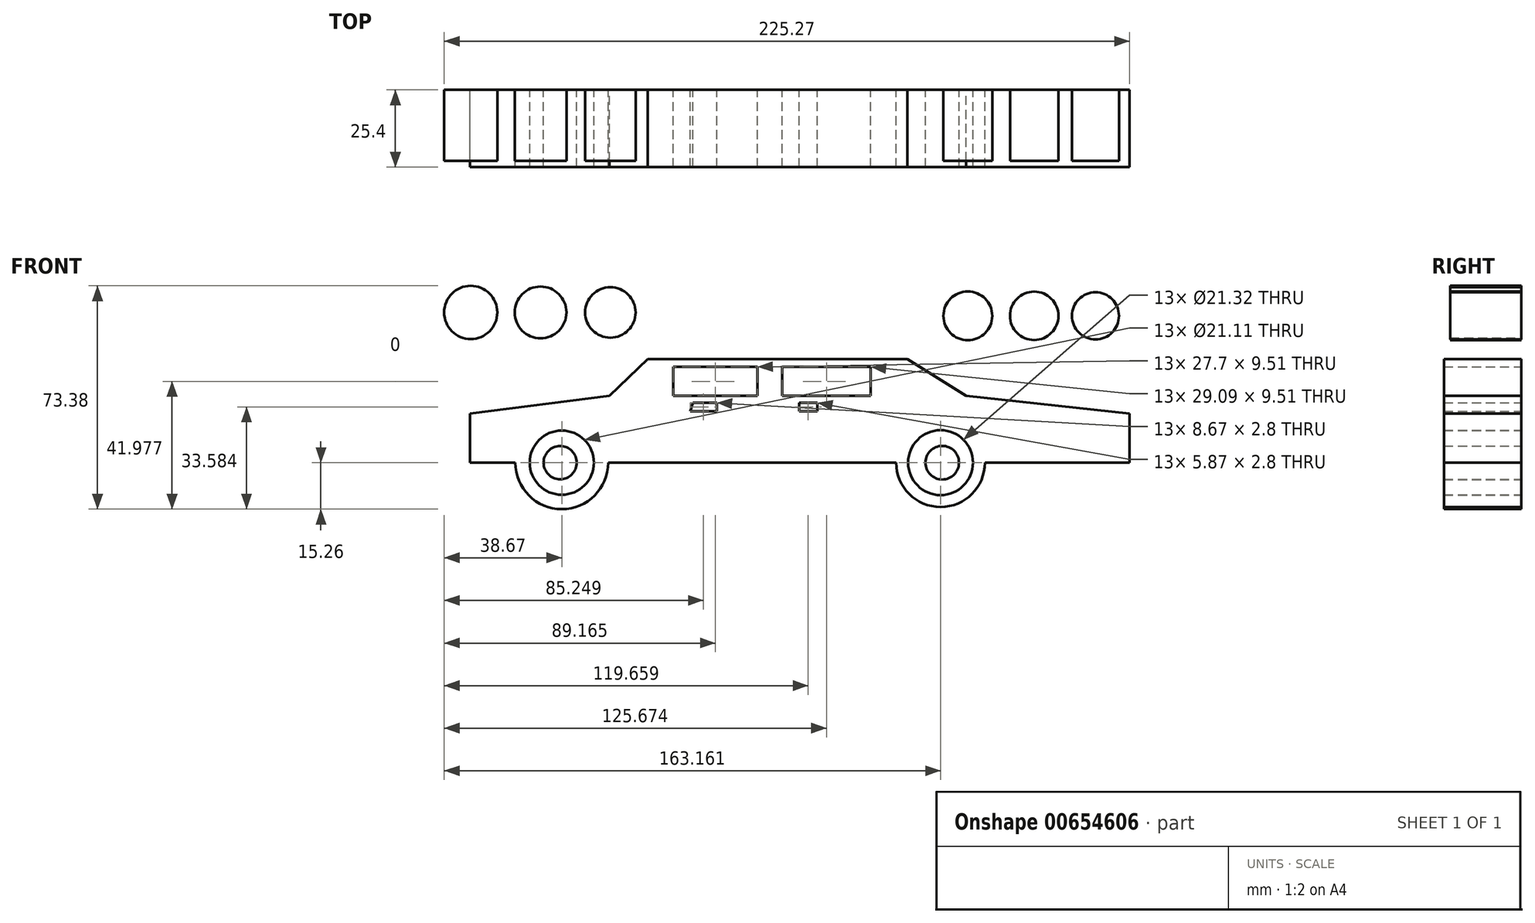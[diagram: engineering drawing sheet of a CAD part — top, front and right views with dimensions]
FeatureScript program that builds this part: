
annotation { "Feature Type Name" : "Feature", "Feature Type Description" : "" }
export const myFeature = defineFeature(function(context is Context, id is Id, definition is map)
    precondition{}
    {
        {
            var Q0;
            Q0=qCreatedBy(makeId("Front.planeOp"),FACE);
            var sketch = newSketch(context, id + "F0", { "sketchPlane" : qUnion([Q0])});
            skLineSegment(sketch, "E0", {"start": v(0, 0) * mm, "end": v(-98.33, 0) * mm});
            skLineSegment(sketch, "E1", {"start": v(-98.33, 0) * mm, "end": v(-98.33, 16.09) * mm});
            skLineSegment(sketch, "E2", {"start": v(-98.33, 16.09) * mm, "end": v(-52.45, 21.96) * mm});
            skLineSegment(sketch, "E3", {"start": v(-52.45, 21.96) * mm, "end": v(-39.87, 34) * mm});
            skLineSegment(sketch, "E4", {"start": v(-39.87, 34) * mm, "end": v(45.46, 34) * mm});
            skLineSegment(sketch, "E5", {"start": v(45.46, 34) * mm, "end": v(64.76, 21.96) * mm});
            skLineSegment(sketch, "E6", {"start": v(64.76, 21.96) * mm, "end": v(118.48, 16.09) * mm});
            skLineSegment(sketch, "E7", {"start": v(118.48, 16.09) * mm, "end": v(118.48, 0) * mm});
            skLineSegment(sketch, "E8", {"start": v(118.48, 0) * mm, "end": v(0, 0) * mm});
            skLineSegment(sketch, "E9", {"start": v(-31.47, 31.47) * mm, "end": v(-31.47, 21.96) * mm});
            skLineSegment(sketch, "E10", {"start": v(-31.47, 21.96) * mm, "end": v(-3.78, 21.96) * mm});
            skLineSegment(sketch, "E11", {"start": v(-3.78, 21.96) * mm, "end": v(-3.78, 31.47) * mm});
            skLineSegment(sketch, "E12", {"start": v(-3.78, 31.47) * mm, "end": v(-31.47, 31.47) * mm});
            skLineSegment(sketch, "E13", {"start": v(4.34, 21.96) * mm, "end": v(33.43, 21.96) * mm});
            skPoint(sketch, "E13.startSnap0", {"position": v(-17.62, 21.96) * mm});
            skLineSegment(sketch, "E14", {"start": v(33.43, 21.96) * mm, "end": v(33.43, 31.47) * mm});
            skLineSegment(sketch, "E15", {"start": v(33.43, 31.47) * mm, "end": v(4.34, 31.47) * mm});
            skLineSegment(sketch, "E16", {"start": v(4.34, 31.47) * mm, "end": v(4.34, 21.96) * mm});
            skCircle(sketch, "E17", {"center": v(-68.12, 0) * mm, "radius": 15.26 * mm});
            skCircle(sketch, "E18", {"center": v(56.37, 0) * mm, "radius": 14.57 * mm});
            skCircle(sketch, "E19", {"center": v(-68.12, 0) * mm, "radius": 10.55 * mm});
            skCircle(sketch, "E20", {"center": v(-68.12, 0) * mm, "radius": 7.02 * mm});
            skCircle(sketch, "E21", {"center": v(56.37, 0) * mm, "radius": 10.66 * mm});
            skCircle(sketch, "E22", {"center": v(56.37, 0) * mm, "radius": 7.08 * mm});
            skLineSegment(sketch, "E23", {"start": v(9.93, 16.93) * mm, "end": v(15.8, 16.93) * mm});
            skLineSegment(sketch, "E24", {"start": v(15.8, 16.93) * mm, "end": v(15.8, 19.72) * mm});
            skLineSegment(sketch, "E25", {"start": v(15.8, 19.72) * mm, "end": v(9.93, 19.72) * mm});
            skLineSegment(sketch, "E26", {"start": v(9.93, 19.72) * mm, "end": v(9.93, 16.93) * mm});
            skLineSegment(sketch, "E27", {"start": v(-25.88, 16.93) * mm, "end": v(-17.2, 16.93) * mm});
            skLineSegment(sketch, "E28", {"start": v(-17.2, 16.93) * mm, "end": v(-17.2, 19.72) * mm});
            skLineSegment(sketch, "E29", {"start": v(-17.2, 19.72) * mm, "end": v(-25.04, 19.72) * mm});
            skLineSegment(sketch, "E30", {"start": v(-25.04, 19.72) * mm, "end": v(-25.88, 16.93) * mm});
            skPoint(sketch, "E31.firstSnap0", {"position": v(-21.12, 19.72) * mm});
            skLineSegment(sketch, "E31.bottom", {"start": v(-21.12, 16.93) * mm, "end": v(-17.2, 16.93) * mm});
            skLineSegment(sketch, "E31.top", {"start": v(-21.12, 19.72) * mm, "end": v(-17.2, 19.72) * mm});
            skLineSegment(sketch, "E31.left", {"start": v(-21.12, 16.93) * mm, "end": v(-21.12, 19.72) * mm});
            skLineSegment(sketch, "E32.bottom", {"start": v(12.87, 19.72) * mm, "end": v(15.8, 19.72) * mm});
            skLineSegment(sketch, "E32.top", {"start": v(12.87, 16.93) * mm, "end": v(15.8, 16.93) * mm});
            skLineSegment(sketch, "E32.left", {"start": v(12.87, 19.72) * mm, "end": v(12.87, 16.93) * mm});
            skLineSegment(sketch, "E32.right", {"start": v(15.8, 19.72) * mm, "end": v(15.8, 16.93) * mm});
            skSolve(sketch);
        }
        {
            var Q0;
            Q0 = qSketchRegion(id + "F0", true);
            extrude(context, id + "F1", {"entities" : qUnion([Q0]), "depth" : 25.4 * mm, "offsetDistance" : 25.4 * mm});
        }
        {
            var Q0;
            Q0=qCreatedBy(makeId("Front.planeOp"),FACE);
            var sketch = newSketch(context, id + "F2", { "sketchPlane" : qUnion([Q0])});
            skCircle(sketch, "E33", {"center": v(-68.68, 0) * mm, "radius": 5.45 * mm});
            skCircle(sketch, "E34", {"center": v(56.93, 0) * mm, "radius": 5.52 * mm});
            skSolve(sketch);
        }
        {
            var Q0;
            Q0 = qSketchRegion(id + "F2", true);
            extrude(context, id + "F3", {"entities" : qUnion([Q0]), "depth" : 25.4 * mm, "offsetDistance" : 25.4 * mm});
        }
        {
            var Q0;
            Q0=qCreatedBy(makeId("Front.planeOp"),FACE);
            var sketch = newSketch(context, id + "F4", { "sketchPlane" : qUnion([Q0])});
            skLineSegment(sketch, "E35", {"start": v(65.32, 22.52) * mm, "end": v(65.32, 48.26) * mm});
            skLineSegment(sketch, "E36", {"start": v(65.32, 48.26) * mm, "end": v(65.32, 22.52) * mm});
            skCircle(sketch, "E37", {"center": v(65.32, 48.26) * mm, "radius": 8.02 * mm});
            skLineSegment(sketch, "E38", {"start": v(-52.17, 22.24) * mm, "end": v(-52.17, 49.38) * mm});
            skLineSegment(sketch, "E39", {"start": v(-52.17, 49.38) * mm, "end": v(-52.17, 22.24) * mm});
            skCircle(sketch, "E40", {"center": v(-52.17, 49.38) * mm, "radius": 8.3 * mm});
            skLineSegment(sketch, "E41", {"start": v(-75.11, 19.16) * mm, "end": v(-75.11, 49.38) * mm});
            skLineSegment(sketch, "E42", {"start": v(-75.11, 49.38) * mm, "end": v(-75.11, 19.16) * mm});
            skLineSegment(sketch, "E43", {"start": v(-98.05, 16.37) * mm, "end": v(-98.05, 49.38) * mm});
            skLineSegment(sketch, "E44", {"start": v(-98.05, 49.38) * mm, "end": v(-98.05, 16.37) * mm});
            skCircle(sketch, "E45", {"center": v(-75.11, 49.38) * mm, "radius": 8.5 * mm});
            skCircle(sketch, "E46", {"center": v(-98.05, 49.38) * mm, "radius": 8.74 * mm});
            skLineSegment(sketch, "E47", {"start": v(87.14, 19.72) * mm, "end": v(87.14, 48.26) * mm});
            skLineSegment(sketch, "E48", {"start": v(87.14, 48.26) * mm, "end": v(87.14, 19.72) * mm});
            skLineSegment(sketch, "E49", {"start": v(107.29, 17.76) * mm, "end": v(107.29, 48.26) * mm});
            skLineSegment(sketch, "E50", {"start": v(107.29, 48.26) * mm, "end": v(107.29, 17.76) * mm});
            skCircle(sketch, "E51", {"center": v(87.14, 48.26) * mm, "radius": 7.95 * mm});
            skCircle(sketch, "E52", {"center": v(107.29, 48.26) * mm, "radius": 7.74 * mm});
            skSolve(sketch);
        }
        {
            var Q0;
            Q0 = qSketchRegion(id + "F4", true);
            extrude(context, id + "F5", {"entities" : qUnion([Q0]), "depth" : 23.37 * mm, "offsetDistance" : 25.4 * mm});
        }
    });
